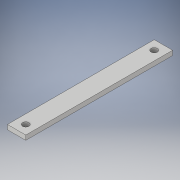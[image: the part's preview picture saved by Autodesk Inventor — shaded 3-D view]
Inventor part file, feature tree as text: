
AUTODESK INVENTOR PART (.ipt)
format: ipt  version: 2019 (Build 230136000, 136)  size: 107,520 bytes
history: native  units: in
note: dims shown in document units (in); Inventor stores cm internally (conversion verified against a paired STEP export)
features: sketch x2, extrude x1, hole x1, projected_geometry x1
ambient origin geometry x8: Origin, YZ Plane, XZ Plane, XY Plane, X Axis, Y Axis, Z Axis, Center Point
bodies: Solid1 (feature_tree)
feature tree (5):
  extrude  "Extrusion1"  Depth=8.0in
  hole  "Hole1"  [1 undecoded]
  sketch  "Sketch1"  dims[d0=1.0in d1=8.0in]
  sketch  "Sketch2"  dims[d2=0.25in d3=0.0in d4=8.0in d5=1.0in d6=0.5in d7=0.5in d8=7.0in d9=0.5in d10=0.35in d11=0.75in d12=0.375in d13=0.25in d14=0.5635in d15=1.0in d16=0.8108in]
  projected_geometry  "Projected Loop1"
note: 1 required parameter value undecoded (feature->parameter linkage not recoverable at this tier; creation-order binding heuristic only, values carry confidence <= 0.55)
